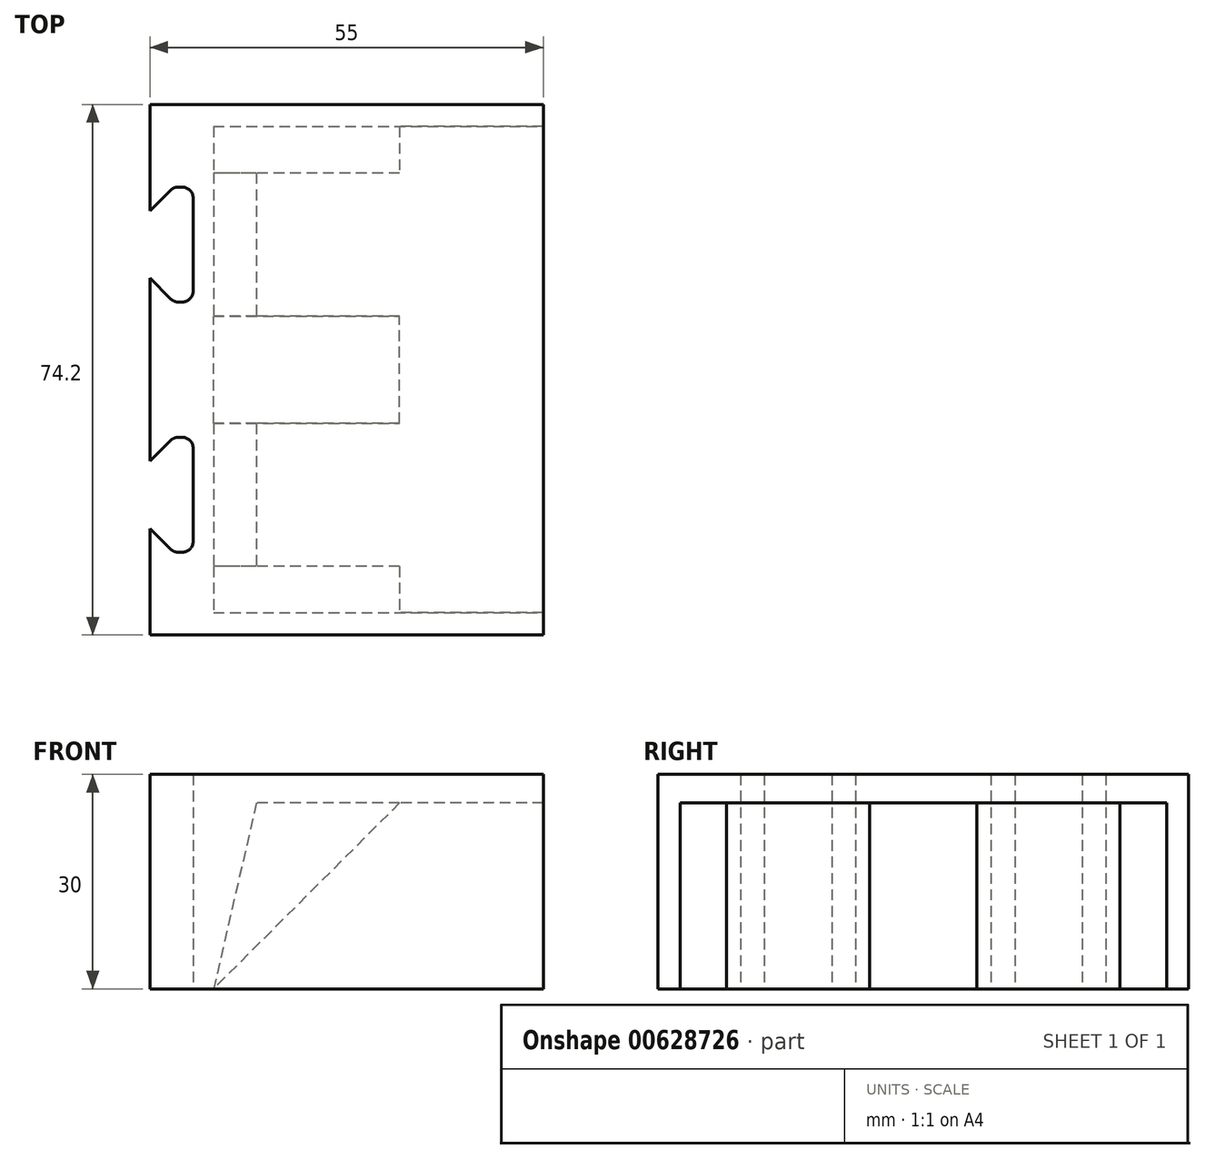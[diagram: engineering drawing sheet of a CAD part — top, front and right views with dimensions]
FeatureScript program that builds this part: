
annotation { "Feature Type Name" : "Feature", "Feature Type Description" : "" }
export const myFeature = defineFeature(function(context is Context, id is Id, definition is map)
    precondition{}
    {
        {
            var Q0;
            Q0=qCreatedBy(makeId("Top.planeOp"),FACE);
            var sketch = newSketch(context, id + "F0", { "sketchPlane" : qUnion([Q0])});
            skLineSegment(sketch, "E0.bottom", {"start": v(90, -35) * mm, "end": v(0, -35) * mm});
            skLineSegment(sketch, "E0.top", {"start": v(90, 35) * mm, "end": v(0, 35) * mm});
            skLineSegment(sketch, "E0.left", {"start": v(90, -35) * mm, "end": v(90, 35) * mm});
            skPoint(sketch, "E0.middle", {"position": v(0, 0) * mm});
            skPoint(sketch, "E1.middle", {"position": v(49.8, 0) * mm});
            skLineSegment(sketch, "E2", {"start": v(0, 0) * mm, "end": v(24, 0) * mm, "construction": true});
            skLineSegment(sketch, "E3", {"start": v(0, 0) * mm, "end": v(0, -14) * mm, "construction": true});
            skLineSegment(sketch, "E4", {"start": v(0, 0) * mm, "end": v(-35, 0) * mm, "construction": true});
            skLineSegment(sketch, "E5.bottom", {"start": v(-5, -19.5) * mm, "end": v(5, -19.5) * mm});
            skLineSegment(sketch, "E5.top", {"start": v(-5, 19.5) * mm, "end": v(5, 19.5) * mm});
            skLineSegment(sketch, "E5.left", {"start": v(-5, -19.5) * mm, "end": v(-5, 19.5) * mm});
            skLineSegment(sketch, "E5.right", {"start": v(5, -19.5) * mm, "end": v(5, 19.5) * mm});
            skLineSegment(sketch, "E6.bottom", {"start": v(-40, -17.25) * mm, "end": v(-30, -17.25) * mm});
            skLineSegment(sketch, "E6.top", {"start": v(-40, 17.25) * mm, "end": v(-30, 17.25) * mm});
            skLineSegment(sketch, "E6.left", {"start": v(-40, -17.25) * mm, "end": v(-40, 17.25) * mm});
            skLineSegment(sketch, "E6.right", {"start": v(-30, -17.25) * mm, "end": v(-30, 17.25) * mm});
            skPoint(sketch, "E6.middle", {"position": v(-35, 0) * mm});
            skLineSegment(sketch, "E7", {"start": v(0, 35) * mm, "end": v(0, 23) * mm});
            skPoint(sketch, "E7.endSnap0", {"position": v(0, 35) * mm});
            skLineSegment(sketch, "E8", {"start": v(0, 23) * mm, "end": v(-50, 23) * mm});
            skLineSegment(sketch, "E9", {"start": v(-50, 23) * mm, "end": v(-50, 0) * mm});
            skLineSegment(sketch, "E10.MirrorCS", {"start": v(-50, -23) * mm, "end": v(-50, 0) * mm});
            skLineSegment(sketch, "E11.MirrorCS", {"start": v(0, -35) * mm, "end": v(0, -23) * mm});
            skLineSegment(sketch, "E12.MirrorCS", {"start": v(0, -23) * mm, "end": v(-50, -23) * mm});
            skPoint(sketch, "E0.right.end.orphan", {"position": v(-90, 35) * mm});
            skPoint(sketch, "E13.orphan", {"position": v(-90, -35) * mm});
            skLineSegment(sketch, "E14.0", {"start": v(92.1, -37.1) * mm, "end": v(92.1, 37.1) * mm});
            skLineSegment(sketch, "E14.1", {"start": v(92.1, -37.1) * mm, "end": v(-2.1, -37.1) * mm});
            skLineSegment(sketch, "E14.2", {"start": v(92.1, 37.1) * mm, "end": v(-2.1, 37.1) * mm});
            skLineSegment(sketch, "E14.3", {"start": v(-2.1, -37.1) * mm, "end": v(-2.1, -25.1) * mm});
            skLineSegment(sketch, "E14.4", {"start": v(-2.1, -25.1) * mm, "end": v(-52.1, -25.1) * mm});
            skLineSegment(sketch, "E14.5", {"start": v(-2.1, 37.1) * mm, "end": v(-2.1, 25.1) * mm});
            skLineSegment(sketch, "E14.6", {"start": v(-2.1, 25.1) * mm, "end": v(-52.1, 25.1) * mm});
            skLineSegment(sketch, "E14.7", {"start": v(-52.1, 25.1) * mm, "end": v(-52.1, 0) * mm});
            skLineSegment(sketch, "E14.8", {"start": v(-52.1, -25.1) * mm, "end": v(-52.1, 0) * mm});
            skLineSegment(sketch, "E15.bottom", {"start": v(-30, 52.75) * mm, "end": v(-40, 52.75) * mm});
            skLineSegment(sketch, "E15.top", {"start": v(-30, 87.25) * mm, "end": v(-40, 87.25) * mm});
            skLineSegment(sketch, "E15.left", {"start": v(-30, 52.75) * mm, "end": v(-30, 87.25) * mm});
            skLineSegment(sketch, "E15.right", {"start": v(-40, 52.75) * mm, "end": v(-40, 87.25) * mm});
            skPoint(sketch, "E15.middle", {"position": v(-35, 70) * mm});
            skLineSegment(sketch, "E16.bottom", {"start": v(-5, 50.5) * mm, "end": v(5, 50.5) * mm});
            skLineSegment(sketch, "E16.top", {"start": v(-5, 89.5) * mm, "end": v(5, 89.5) * mm});
            skLineSegment(sketch, "E16.left", {"start": v(-5, 50.5) * mm, "end": v(-5, 89.5) * mm});
            skLineSegment(sketch, "E16.right", {"start": v(5, 50.5) * mm, "end": v(5, 89.5) * mm});
            skPoint(sketch, "E16.middle", {"position": v(0, 70) * mm});
            skPoint(sketch, "E16.middle.positionSnap0", {"position": v(-30, 70) * mm});
            skPoint(sketch, "E16.centerSnap0", {"position": v(-30, 70) * mm});
            skLineSegment(sketch, "E17", {"start": v(-35, 0) * mm, "end": v(-35, 70) * mm, "construction": true});
            skCircle(sketch, "E18", {"center": v(0, -14) * mm, "radius": 2 * mm});
            skLineSegment(sketch, "E19", {"start": v(-35, 0) * mm, "end": v(-35, -11.75) * mm, "construction": true});
            skCircle(sketch, "E20", {"center": v(-35, -11.75) * mm, "radius": 2 * mm});
            skCircle(sketch, "E21.MirrorC", {"center": v(-35, 11.75) * mm, "radius": 2 * mm});
            skCircle(sketch, "E22.MirrorC", {"center": v(0, 14) * mm, "radius": 2 * mm});
            skLineSegment(sketch, "E23", {"start": v(-35, 70) * mm, "end": v(-35, 81.75) * mm, "construction": true});
            skLineSegment(sketch, "E24", {"start": v(0, 70) * mm, "end": v(0, 84) * mm, "construction": true});
            skCircle(sketch, "E25", {"center": v(-35, 81.75) * mm, "radius": 2 * mm});
            skCircle(sketch, "E26", {"center": v(0, 84) * mm, "radius": 2 * mm});
            skLineSegment(sketch, "E27", {"start": v(-35, 70) * mm, "end": v(-30, 70) * mm, "construction": true});
            skCircle(sketch, "E28.MirrorC", {"center": v(-35, 58.25) * mm, "radius": 2 * mm});
            skCircle(sketch, "E29.MirrorC", {"center": v(0, 56) * mm, "radius": 2 * mm});
            skLineSegment(sketch, "E30", {"start": v(90, -35) * mm, "end": v(92.1, -35) * mm});
            skLineSegment(sketch, "E31", {"start": v(90, 35) * mm, "end": v(92.1, 35) * mm});
            skLineSegment(sketch, "E32", {"start": v(-2.1, 37.1) * mm, "end": v(-6.1, 37.1) * mm});
            skLineSegment(sketch, "E33", {"start": v(-6.1, 37.1) * mm, "end": v(-6.1, 25.1) * mm});
            skLineSegment(sketch, "E34", {"start": v(-2.1, -37.1) * mm, "end": v(-6.1, -37.1) * mm});
            skLineSegment(sketch, "E35", {"start": v(-6.1, -37.1) * mm, "end": v(-6.1, -25.1) * mm});
            skLineSegment(sketch, "E36", {"start": v(-41, 23) * mm, "end": v(-41, 11) * mm});
            skLineSegment(sketch, "E37", {"start": v(-41, 11) * mm, "end": v(-50, 11) * mm});
            skPoint(sketch, "E38.end.orphan", {"position": v(-41, 14.45) * mm});
            skLineSegment(sketch, "E39.MirrorCS", {"start": v(-41, -11) * mm, "end": v(-50, -11) * mm});
            skLineSegment(sketch, "E40.MirrorCS", {"start": v(-41, -23) * mm, "end": v(-41, -11) * mm});
            skLineSegment(sketch, "E41", {"start": v(90, -35) * mm, "end": v(90, -37.1) * mm});
            skLineSegment(sketch, "E42", {"start": v(90, 35) * mm, "end": v(90, 37.1) * mm});
            skLineSegment(sketch, "E43.bottom", {"start": v(90, 35) * mm, "end": v(86, 35) * mm});
            skLineSegment(sketch, "E43.left", {"start": v(90, 35) * mm, "end": v(90, 23) * mm});
            skLineSegment(sketch, "E44.bottom", {"start": v(90, -35) * mm, "end": v(86, -35) * mm});
            skLineSegment(sketch, "E44.left", {"start": v(90, -35) * mm, "end": v(90, -23) * mm});
            skLineSegment(sketch, "E45.bottom", {"start": v(86, -35) * mm, "end": v(80, -35) * mm});
            skLineSegment(sketch, "E46.bottom", {"start": v(86, 35) * mm, "end": v(80, 35) * mm});
            skLineSegment(sketch, "E47.bottom", {"start": v(0, 23) * mm, "end": v(7, 23) * mm});
            skLineSegment(sketch, "E47.top", {"start": v(0, 35) * mm, "end": v(12, 35) * mm});
            skLineSegment(sketch, "E47.left", {"start": v(0, 23) * mm, "end": v(0, 35) * mm});
            skLineSegment(sketch, "E47.right", {"start": v(12, 28) * mm, "end": v(12, 35) * mm});
            skLineSegment(sketch, "E48.bottom", {"start": v(0, -35) * mm, "end": v(12, -35) * mm});
            skLineSegment(sketch, "E48.top", {"start": v(0, -23) * mm, "end": v(7, -23) * mm});
            skLineSegment(sketch, "E48.right", {"start": v(12, -35) * mm, "end": v(12, -28) * mm});
            skCircle(sketch, "E49", {"center": v(6, -29) * mm, "radius": 2 * mm});
            skPoint(sketch, "E49.centerSnap0", {"position": v(6, -35) * mm});
            skPoint(sketch, "E49.centerSnap1", {"position": v(0, -29) * mm});
            skPoint(sketch, "E50.visualSharp", {"position": v(12, -23) * mm});
            skArc(sketch, "E50.filletArc", {"start": v(12, -28) * mm, "mid": v(10.54, -24.46) * mm, "end": v(7, -23) * mm});
            skPoint(sketch, "E51.visualSharp", {"position": v(12, 23) * mm});
            skArc(sketch, "E51.filletArc", {"start": v(7, 23) * mm, "mid": v(10.54, 24.46) * mm, "end": v(12, 28) * mm});
            skCircle(sketch, "E52.MirrorC", {"center": v(6, 29) * mm, "radius": 2 * mm});
            skCircle(sketch, "E53", {"center": v(6, 29) * mm, "radius": 4.5 * mm});
            skCircle(sketch, "E54.MirrorC", {"center": v(6, -29) * mm, "radius": 4.5 * mm});
            skCircle(sketch, "E55", {"center": v(0, 14) * mm, "radius": 6 * mm});
            skCircle(sketch, "E56", {"center": v(-35, 11.75) * mm, "radius": 6 * mm});
            skCircle(sketch, "E57", {"center": v(-35, -11.75) * mm, "radius": 6 * mm});
            skCircle(sketch, "E58", {"center": v(0, -14) * mm, "radius": 6 * mm});
            skLineSegment(sketch, "E59", {"start": v(-6.1, 25.1) * mm, "end": v(-6.08, 23) * mm});
            skLineSegment(sketch, "E60", {"start": v(-6.1, -25.1) * mm, "end": v(-6.1, -23) * mm});
            skLineSegment(sketch, "E61", {"start": v(-47.66, 23) * mm, "end": v(-47.66, 18) * mm, "construction": true});
            skLineSegment(sketch, "E62", {"start": v(-50, 18) * mm, "end": v(-45, 18) * mm, "construction": true});
            skCircle(sketch, "E63", {"center": v(-45, 18) * mm, "radius": 2.25 * mm});
            skCircle(sketch, "E64.MirrorC", {"center": v(-45, -18) * mm, "radius": 2.25 * mm});
            skCircle(sketch, "E65.MirrorC", {"center": v(-25, 18) * mm, "radius": 2.25 * mm});
            skCircle(sketch, "E66.MirrorC", {"center": v(-25, -18) * mm, "radius": 2.25 * mm});
            skCircle(sketch, "E67.MirrorC", {"center": v(28.54, -17.75) * mm, "radius": 2.25 * mm});
            skLineSegment(sketch, "E68.bottom", {"start": v(34.04, -22.75) * mm, "end": v(23.04, -22.75) * mm});
            skLineSegment(sketch, "E68.top", {"start": v(34.04, -12.75) * mm, "end": v(23.04, -12.75) * mm});
            skLineSegment(sketch, "E68.left", {"start": v(36.04, -20.75) * mm, "end": v(36.04, -14.75) * mm});
            skLineSegment(sketch, "E68.right", {"start": v(21.04, -20.75) * mm, "end": v(21.04, -14.75) * mm});
            skLineSegment(sketch, "E69.0", {"start": v(36.44, -12.35) * mm, "end": v(20.64, -12.35) * mm});
            skLineSegment(sketch, "E69.1", {"start": v(36.44, -23.15) * mm, "end": v(36.44, -12.35) * mm});
            skLineSegment(sketch, "E69.2", {"start": v(36.44, -23.15) * mm, "end": v(20.64, -23.15) * mm});
            skLineSegment(sketch, "E69.3", {"start": v(20.64, -23.15) * mm, "end": v(20.64, -12.35) * mm});
            skPoint(sketch, "E70.visualSharp", {"position": v(21.04, -12.75) * mm});
            skArc(sketch, "E70.filletArc", {"start": v(23.04, -12.75) * mm, "mid": v(21.62, -13.33) * mm, "end": v(21.04, -14.75) * mm});
            skPoint(sketch, "E71.visualSharp", {"position": v(36.04, -12.75) * mm});
            skArc(sketch, "E71.filletArc", {"start": v(36.04, -14.75) * mm, "mid": v(35.45, -13.33) * mm, "end": v(34.04, -12.75) * mm});
            skPoint(sketch, "E72.visualSharp", {"position": v(36.04, -22.75) * mm});
            skArc(sketch, "E72.filletArc", {"start": v(34.04, -22.75) * mm, "mid": v(35.45, -22.16) * mm, "end": v(36.04, -20.75) * mm});
            skPoint(sketch, "E73.visualSharp", {"position": v(21.04, -22.75) * mm});
            skArc(sketch, "E73.filletArc", {"start": v(21.04, -20.75) * mm, "mid": v(21.62, -22.16) * mm, "end": v(23.04, -22.75) * mm});
            skArc(sketch, "E74.0", {"start": v(39.54, -14.75) * mm, "mid": v(37.93, -10.86) * mm, "end": v(34.04, -9.25) * mm});
            skLineSegment(sketch, "E74.1", {"start": v(39.54, -20.75) * mm, "end": v(39.54, -14.75) * mm});
            skLineSegment(sketch, "E74.2", {"start": v(34.04, -9.25) * mm, "end": v(23.04, -9.25) * mm});
            skArc(sketch, "E74.3", {"start": v(34.04, -26.25) * mm, "mid": v(37.93, -24.64) * mm, "end": v(39.54, -20.75) * mm});
            skArc(sketch, "E74.4", {"start": v(23.04, -9.25) * mm, "mid": v(19.15, -10.86) * mm, "end": v(17.54, -14.75) * mm});
            skLineSegment(sketch, "E74.5", {"start": v(17.54, -20.75) * mm, "end": v(17.54, -14.75) * mm});
            skArc(sketch, "E74.6", {"start": v(17.54, -20.75) * mm, "mid": v(19.15, -24.64) * mm, "end": v(23.04, -26.25) * mm});
            skLineSegment(sketch, "E74.7", {"start": v(34.04, -26.25) * mm, "end": v(23.04, -26.25) * mm});
            skLineSegment(sketch, "E75", {"start": v(45, 37.1) * mm, "end": v(45, -37.1) * mm});
            skLineSegment(sketch, "E76", {"start": v(45, 31.57) * mm, "end": v(68, 31.57) * mm, "construction": true});
            skLineSegment(sketch, "E77", {"start": v(68, 35) * mm, "end": v(68, -35) * mm});
            skLineSegment(sketch, "E78", {"start": v(12, -28) * mm, "end": v(12, 28) * mm});
            skLineSegment(sketch, "E79", {"start": v(12, 35) * mm, "end": v(12, 37.1) * mm});
            skLineSegment(sketch, "E80", {"start": v(68, 35) * mm, "end": v(68, 37.1) * mm});
            skLineSegment(sketch, "E81", {"start": v(68, 31.57) * mm, "end": v(70.1, 31.57) * mm, "construction": true});
            skLineSegment(sketch, "E82", {"start": v(70.1, 37.1) * mm, "end": v(70.1, -37.1) * mm});
            skLineSegment(sketch, "E83", {"start": v(12, -35) * mm, "end": v(12, -37.1) * mm});
            skLineSegment(sketch, "E84", {"start": v(72.96, 0) * mm, "end": v(72.96, 17.5) * mm, "construction": true});
            skPoint(sketch, "E84.startSnap0", {"position": v(70.1, 0) * mm});
            skLineSegment(sketch, "E85", {"start": v(70.1, 13.5) * mm, "end": v(73.34, 10.26) * mm});
            skPoint(sketch, "E86.end.orphan", {"position": v(71.21, 13.5) * mm});
            skPoint(sketch, "E86.start.orphan", {"position": v(71.21, 17.5) * mm});
            skLineSegment(sketch, "E87", {"start": v(74.05, 9.96) * mm, "end": v(74.64, 9.96) * mm});
            skLineSegment(sketch, "E88", {"start": v(72.96, 17.5) * mm, "end": v(71.21, 17.5) * mm, "construction": true});
            skLineSegment(sketch, "E89.MirrorCS", {"start": v(70.1, 21.5) * mm, "end": v(73.34, 24.74) * mm});
            skLineSegment(sketch, "E90.MirrorCS", {"start": v(74.05, 25.04) * mm, "end": v(74.64, 25.04) * mm});
            skLineSegment(sketch, "E91", {"start": v(75.64, 24.04) * mm, "end": v(75.64, 10.96) * mm});
            skPoint(sketch, "E92.visualSharp", {"position": v(75.64, 25.04) * mm});
            skArc(sketch, "E92.filletArc", {"start": v(75.64, 24.04) * mm, "mid": v(75.34, 24.74) * mm, "end": v(74.64, 25.04) * mm});
            skPoint(sketch, "E93.visualSharp", {"position": v(73.64, 25.04) * mm});
            skArc(sketch, "E93.filletArc", {"start": v(74.05, 25.04) * mm, "mid": v(73.67, 24.96) * mm, "end": v(73.34, 24.74) * mm});
            skPoint(sketch, "E94.visualSharp", {"position": v(73.64, 9.96) * mm});
            skArc(sketch, "E94.filletArc", {"start": v(73.34, 10.26) * mm, "mid": v(73.67, 10.04) * mm, "end": v(74.05, 9.96) * mm});
            skPoint(sketch, "E95.visualSharp", {"position": v(75.64, 9.96) * mm});
            skArc(sketch, "E95.filletArc", {"start": v(74.64, 9.96) * mm, "mid": v(75.34, 10.26) * mm, "end": v(75.64, 10.96) * mm});
            skLineSegment(sketch, "E96.MirrorCS", {"start": v(70.1, -13.5) * mm, "end": v(73.34, -10.26) * mm});
            skArc(sketch, "E97.MirrorCS", {"start": v(73.34, -10.26) * mm, "mid": v(73.67, -10.04) * mm, "end": v(74.05, -9.96) * mm});
            skLineSegment(sketch, "E98.MirrorCS", {"start": v(74.05, -9.96) * mm, "end": v(74.64, -9.96) * mm});
            skArc(sketch, "E99.MirrorCS", {"start": v(74.64, -9.96) * mm, "mid": v(75.34, -10.26) * mm, "end": v(75.64, -10.96) * mm});
            skLineSegment(sketch, "E100.MirrorCS", {"start": v(75.64, -24.04) * mm, "end": v(75.64, -10.96) * mm});
            skLineSegment(sketch, "E101.MirrorCS", {"start": v(70.1, -21.5) * mm, "end": v(73.34, -24.74) * mm});
            skArc(sketch, "E102.MirrorCS", {"start": v(74.05, -25.04) * mm, "mid": v(73.67, -24.96) * mm, "end": v(73.34, -24.74) * mm});
            skLineSegment(sketch, "E103.MirrorCS", {"start": v(74.05, -25.04) * mm, "end": v(74.64, -25.04) * mm});
            skArc(sketch, "E104.MirrorCS", {"start": v(75.64, -24.04) * mm, "mid": v(75.34, -24.74) * mm, "end": v(74.64, -25.04) * mm});
            skLineSegment(sketch, "E105", {"start": v(68, -35) * mm, "end": v(56.64, -23.64) * mm, "construction": true});
            skArc(sketch, "E106.MirrorCS", {"start": v(43.26, -40.34) * mm, "mid": v(43.04, -40.67) * mm, "end": v(42.96, -41.05) * mm});
            skArc(sketch, "E107.MirrorCS", {"start": v(58.04, -41.05) * mm, "mid": v(57.96, -40.67) * mm, "end": v(57.74, -40.34) * mm});
            skArc(sketch, "E108.MirrorCS", {"start": v(42.96, -41.64) * mm, "mid": v(43.26, -42.34) * mm, "end": v(43.96, -42.64) * mm});
            skArc(sketch, "E109.MirrorCS", {"start": v(57.04, -42.64) * mm, "mid": v(57.74, -42.34) * mm, "end": v(58.04, -41.64) * mm});
            skLineSegment(sketch, "E110.MirrorCS", {"start": v(42.96, -41.05) * mm, "end": v(42.96, -41.64) * mm});
            skLineSegment(sketch, "E111.MirrorCS", {"start": v(58.04, -41.05) * mm, "end": v(58.04, -41.64) * mm});
            skLineSegment(sketch, "E112.MirrorCS", {"start": v(57.04, -42.64) * mm, "end": v(43.96, -42.64) * mm});
            skLineSegment(sketch, "E113.MirrorCS", {"start": v(46.5, -37.1) * mm, "end": v(43.26, -40.34) * mm});
            skLineSegment(sketch, "E114.MirrorCS", {"start": v(54.5, -37.1) * mm, "end": v(57.74, -40.34) * mm});
            skLineSegment(sketch, "E115", {"start": v(36.04, -37.1) * mm, "end": v(36.04, -40.15) * mm, "construction": true});
            skLineSegment(sketch, "E116.MirrorCS", {"start": v(14.04, -41.05) * mm, "end": v(14.04, -41.64) * mm});
            skArc(sketch, "E117.MirrorCS", {"start": v(14.04, -41.05) * mm, "mid": v(14.12, -40.67) * mm, "end": v(14.33, -40.34) * mm});
            skLineSegment(sketch, "E118.MirrorCS", {"start": v(29.11, -41.05) * mm, "end": v(29.11, -41.64) * mm});
            skArc(sketch, "E119.MirrorCS", {"start": v(28.82, -40.34) * mm, "mid": v(29.04, -40.67) * mm, "end": v(29.11, -41.05) * mm});
            skArc(sketch, "E120.MirrorCS", {"start": v(15.04, -42.64) * mm, "mid": v(14.33, -42.34) * mm, "end": v(14.04, -41.64) * mm});
            skLineSegment(sketch, "E121.MirrorCS", {"start": v(15.04, -42.64) * mm, "end": v(28.11, -42.64) * mm});
            skArc(sketch, "E122.MirrorCS", {"start": v(29.11, -41.64) * mm, "mid": v(28.82, -42.34) * mm, "end": v(28.11, -42.64) * mm});
            skLineSegment(sketch, "E123.MirrorCS", {"start": v(17.58, -37.1) * mm, "end": v(14.33, -40.34) * mm});
            skLineSegment(sketch, "E124.MirrorCS", {"start": v(25.58, -37.1) * mm, "end": v(28.82, -40.34) * mm});
            skLineSegment(sketch, "E125", {"start": v(28.54, -17.75) * mm, "end": v(28.54, 0) * mm, "construction": true});
            skLineSegment(sketch, "E126", {"start": v(28.54, 0) * mm, "end": v(56.04, 0) * mm, "construction": true});
            skLineSegment(sketch, "E127.bottom", {"start": v(53.54, 20) * mm, "end": v(58.54, 20) * mm});
            skLineSegment(sketch, "E127.top", {"start": v(53.54, -20) * mm, "end": v(58.54, -20) * mm});
            skLineSegment(sketch, "E127.left", {"start": v(53.54, 20) * mm, "end": v(53.54, -20) * mm});
            skLineSegment(sketch, "E127.right", {"start": v(58.54, 20) * mm, "end": v(58.54, -20) * mm});
            skPoint(sketch, "E127.middle", {"position": v(56.04, 0) * mm});
            skLineSegment(sketch, "E128", {"start": v(28.54, -17.75) * mm, "end": v(28.54, -35) * mm, "construction": true});
            skPoint(sketch, "E128.endSnap0", {"position": v(28.54, -26.25) * mm});
            skLineSegment(sketch, "E129", {"start": v(28.54, -17.75) * mm, "end": v(12, -17.75) * mm, "construction": true});
            skLineSegment(sketch, "E130", {"start": v(12, 17.54) * mm, "end": v(28.54, 17.54) * mm, "construction": true});
            skLineSegment(sketch, "E131", {"start": v(28.54, 17.54) * mm, "end": v(28.54, 35) * mm, "construction": true});
            skArc(sketch, "E132.MirrorCS", {"start": v(36.04, 14.75) * mm, "mid": v(35.45, 13.33) * mm, "end": v(34.04, 12.75) * mm});
            skArc(sketch, "E133.MirrorCS", {"start": v(23.04, 12.75) * mm, "mid": v(21.62, 13.33) * mm, "end": v(21.04, 14.75) * mm});
            skArc(sketch, "E134.MirrorCS", {"start": v(21.04, 20.75) * mm, "mid": v(21.62, 22.16) * mm, "end": v(23.04, 22.75) * mm});
            skArc(sketch, "E135.MirrorCS", {"start": v(34.04, 22.75) * mm, "mid": v(35.45, 22.16) * mm, "end": v(36.04, 20.75) * mm});
            skArc(sketch, "E136.MirrorCS", {"start": v(23.04, 9.25) * mm, "mid": v(19.15, 10.86) * mm, "end": v(17.54, 14.75) * mm});
            skLineSegment(sketch, "E137.MirrorCS", {"start": v(34.04, 9.25) * mm, "end": v(23.04, 9.25) * mm});
            skPoint(sketch, "E138.MirrorP", {"position": v(36.04, 12.75) * mm});
            skArc(sketch, "E139.MirrorCS", {"start": v(34.04, 26.25) * mm, "mid": v(37.93, 24.64) * mm, "end": v(39.54, 20.75) * mm});
            skArc(sketch, "E140.MirrorCS", {"start": v(17.54, 20.75) * mm, "mid": v(19.15, 24.64) * mm, "end": v(23.04, 26.25) * mm});
            skPoint(sketch, "E141.MirrorP", {"position": v(28.54, 17.75) * mm});
            skLineSegment(sketch, "E142.MirrorCS", {"start": v(36.44, 23.15) * mm, "end": v(20.64, 23.15) * mm});
            skPoint(sketch, "E143.MirrorP", {"position": v(21.04, 12.75) * mm});
            skLineSegment(sketch, "E144.MirrorCS", {"start": v(34.04, 26.25) * mm, "end": v(23.04, 26.25) * mm});
            skPoint(sketch, "E145.MirrorP", {"position": v(21.04, 22.75) * mm});
            skLineSegment(sketch, "E146.MirrorCS", {"start": v(20.64, 23.15) * mm, "end": v(20.64, 12.35) * mm});
            skLineSegment(sketch, "E147.MirrorCS", {"start": v(36.44, 12.35) * mm, "end": v(20.64, 12.35) * mm});
            skLineSegment(sketch, "E148.MirrorCS", {"start": v(17.54, 20.75) * mm, "end": v(17.54, 14.75) * mm});
            skCircle(sketch, "E149.MirrorC", {"center": v(28.54, 17.75) * mm, "radius": 2.25 * mm});
            skPoint(sketch, "E150.MirrorP", {"position": v(28.54, 26.25) * mm});
            skPoint(sketch, "E151.MirrorP", {"position": v(36.04, 22.75) * mm});
            skLineSegment(sketch, "E152.MirrorCS", {"start": v(21.04, 20.75) * mm, "end": v(21.04, 14.75) * mm});
            skLineSegment(sketch, "E153.MirrorCS", {"start": v(39.54, 20.75) * mm, "end": v(39.54, 14.75) * mm});
            skLineSegment(sketch, "E154.MirrorCS", {"start": v(36.44, 23.15) * mm, "end": v(36.44, 12.35) * mm});
            skLineSegment(sketch, "E155.MirrorCS", {"start": v(34.04, 22.75) * mm, "end": v(23.04, 22.75) * mm});
            skArc(sketch, "E156.MirrorCS", {"start": v(39.54, 14.75) * mm, "mid": v(37.93, 10.86) * mm, "end": v(34.04, 9.25) * mm});
            skLineSegment(sketch, "E157.MirrorCS", {"start": v(34.04, 12.75) * mm, "end": v(23.04, 12.75) * mm});
            skLineSegment(sketch, "E158.MirrorCS", {"start": v(36.04, 20.75) * mm, "end": v(36.04, 14.75) * mm});
            skArc(sketch, "E159.MirrorCS", {"start": v(29.11, 41.64) * mm, "mid": v(28.82, 42.34) * mm, "end": v(28.11, 42.64) * mm});
            skArc(sketch, "E160.MirrorCS", {"start": v(28.82, 40.34) * mm, "mid": v(29.04, 40.67) * mm, "end": v(29.11, 41.05) * mm});
            skArc(sketch, "E161.MirrorCS", {"start": v(15.04, 42.64) * mm, "mid": v(14.33, 42.34) * mm, "end": v(14.04, 41.64) * mm});
            skArc(sketch, "E162.MirrorCS", {"start": v(14.04, 41.05) * mm, "mid": v(14.12, 40.67) * mm, "end": v(14.33, 40.34) * mm});
            skArc(sketch, "E163.MirrorCS", {"start": v(57.04, 42.64) * mm, "mid": v(57.74, 42.34) * mm, "end": v(58.04, 41.64) * mm});
            skArc(sketch, "E164.MirrorCS", {"start": v(58.04, 41.05) * mm, "mid": v(57.96, 40.67) * mm, "end": v(57.74, 40.34) * mm});
            skLineSegment(sketch, "E165.MirrorCS", {"start": v(42.96, 41.05) * mm, "end": v(42.96, 41.64) * mm});
            skLineSegment(sketch, "E166.MirrorCS", {"start": v(58.04, 41.05) * mm, "end": v(58.04, 41.64) * mm});
            skLineSegment(sketch, "E167.MirrorCS", {"start": v(14.04, 41.05) * mm, "end": v(14.04, 41.64) * mm});
            skLineSegment(sketch, "E168.MirrorCS", {"start": v(29.11, 41.05) * mm, "end": v(29.11, 41.64) * mm});
            skArc(sketch, "E169.MirrorCS", {"start": v(42.96, 41.64) * mm, "mid": v(43.26, 42.34) * mm, "end": v(43.96, 42.64) * mm});
            skArc(sketch, "E170.MirrorCS", {"start": v(43.26, 40.34) * mm, "mid": v(43.04, 40.67) * mm, "end": v(42.96, 41.05) * mm});
            skLineSegment(sketch, "E171.MirrorCS", {"start": v(57.04, 42.64) * mm, "end": v(43.96, 42.64) * mm});
            skLineSegment(sketch, "E172.MirrorCS", {"start": v(15.04, 42.64) * mm, "end": v(28.11, 42.64) * mm});
            skLineSegment(sketch, "E173.MirrorCS", {"start": v(17.58, 37.1) * mm, "end": v(14.33, 40.34) * mm});
            skLineSegment(sketch, "E174.MirrorCS", {"start": v(25.58, 37.1) * mm, "end": v(28.82, 40.34) * mm});
            skLineSegment(sketch, "E175.MirrorCS", {"start": v(46.5, 37.1) * mm, "end": v(43.26, 40.34) * mm});
            skLineSegment(sketch, "E176.MirrorCS", {"start": v(54.5, 37.1) * mm, "end": v(57.74, 40.34) * mm});
            skLineSegment(sketch, "E177", {"start": v(92.1, 37.1) * mm, "end": v(125.1, 37.1) * mm});
            skLineSegment(sketch, "E178", {"start": v(125.1, 37.1) * mm, "end": v(125.1, -37.1) * mm});
            skLineSegment(sketch, "E179", {"start": v(125.1, -37.1) * mm, "end": v(92.1, -37.1) * mm});
            skLineSegment(sketch, "E180", {"start": v(125.1, 30.14) * mm, "end": v(123, 30.14) * mm, "construction": true});
            skLineSegment(sketch, "E181.0", {"start": v(70.1, 12.8) * mm, "end": v(72.99, 9.9) * mm});
            skArc(sketch, "E181.1", {"start": v(72.99, 9.9) * mm, "mid": v(73.48, 9.58) * mm, "end": v(74.05, 9.46) * mm});
            skLineSegment(sketch, "E181.2", {"start": v(74.05, 9.46) * mm, "end": v(74.64, 9.46) * mm});
            skArc(sketch, "E181.3", {"start": v(74.64, 9.46) * mm, "mid": v(75.7, 9.9) * mm, "end": v(76.14, 10.96) * mm});
            skLineSegment(sketch, "E181.4", {"start": v(76.14, 24.04) * mm, "end": v(76.14, 10.96) * mm});
            skLineSegment(sketch, "E181.5", {"start": v(70.1, 22.2) * mm, "end": v(72.99, 25.1) * mm});
            skArc(sketch, "E181.6", {"start": v(74.05, 25.54) * mm, "mid": v(73.48, 25.42) * mm, "end": v(72.99, 25.1) * mm});
            skLineSegment(sketch, "E181.7", {"start": v(74.05, 25.54) * mm, "end": v(74.64, 25.54) * mm});
            skArc(sketch, "E181.8", {"start": v(76.14, 24.04) * mm, "mid": v(75.7, 25.1) * mm, "end": v(74.64, 25.54) * mm});
            skLineSegment(sketch, "E182.MirrorCS", {"start": v(70.1, -12.8) * mm, "end": v(72.99, -9.9) * mm});
            skArc(sketch, "E183.MirrorCS", {"start": v(72.99, -9.9) * mm, "mid": v(73.48, -9.58) * mm, "end": v(74.05, -9.46) * mm});
            skLineSegment(sketch, "E184.MirrorCS", {"start": v(74.05, -9.46) * mm, "end": v(74.64, -9.46) * mm});
            skArc(sketch, "E185.MirrorCS", {"start": v(74.64, -9.46) * mm, "mid": v(75.7, -9.9) * mm, "end": v(76.14, -10.96) * mm});
            skLineSegment(sketch, "E186.MirrorCS", {"start": v(76.14, -24.04) * mm, "end": v(76.14, -10.96) * mm});
            skArc(sketch, "E187.MirrorCS", {"start": v(76.14, -24.04) * mm, "mid": v(75.7, -25.1) * mm, "end": v(74.64, -25.54) * mm});
            skLineSegment(sketch, "E188.MirrorCS", {"start": v(74.05, -25.54) * mm, "end": v(74.64, -25.54) * mm});
            skArc(sketch, "E189.MirrorCS", {"start": v(74.05, -25.54) * mm, "mid": v(73.48, -25.42) * mm, "end": v(72.99, -25.1) * mm});
            skLineSegment(sketch, "E190.MirrorCS", {"start": v(70.1, -22.2) * mm, "end": v(72.99, -25.1) * mm});
            skLineSegment(sketch, "E191.0", {"start": v(45.8, -37.1) * mm, "end": v(42.9, -39.99) * mm});
            skArc(sketch, "E191.1", {"start": v(42.9, -39.99) * mm, "mid": v(42.58, -40.48) * mm, "end": v(42.46, -41.05) * mm});
            skLineSegment(sketch, "E191.2", {"start": v(42.46, -41.05) * mm, "end": v(42.46, -41.64) * mm});
            skArc(sketch, "E191.3", {"start": v(42.46, -41.64) * mm, "mid": v(42.9, -42.7) * mm, "end": v(43.96, -43.14) * mm});
            skLineSegment(sketch, "E191.4", {"start": v(57.04, -43.14) * mm, "end": v(43.96, -43.14) * mm});
            skLineSegment(sketch, "E191.5", {"start": v(55.2, -37.1) * mm, "end": v(58.1, -39.99) * mm});
            skArc(sketch, "E191.6", {"start": v(58.54, -41.05) * mm, "mid": v(58.42, -40.48) * mm, "end": v(58.1, -39.99) * mm});
            skLineSegment(sketch, "E191.7", {"start": v(58.54, -41.05) * mm, "end": v(58.54, -41.64) * mm});
            skArc(sketch, "E191.8", {"start": v(57.04, -43.14) * mm, "mid": v(58.1, -42.7) * mm, "end": v(58.54, -41.64) * mm});
            skLineSegment(sketch, "E192.MirrorCS", {"start": v(26.28, -37.1) * mm, "end": v(29.17, -39.99) * mm});
            skArc(sketch, "E193.MirrorCS", {"start": v(29.17, -39.99) * mm, "mid": v(29.5, -40.48) * mm, "end": v(29.61, -41.05) * mm});
            skLineSegment(sketch, "E194.MirrorCS", {"start": v(29.61, -41.05) * mm, "end": v(29.61, -41.64) * mm});
            skArc(sketch, "E195.MirrorCS", {"start": v(29.61, -41.64) * mm, "mid": v(29.17, -42.7) * mm, "end": v(28.11, -43.14) * mm});
            skLineSegment(sketch, "E196.MirrorCS", {"start": v(15.04, -43.14) * mm, "end": v(28.11, -43.14) * mm});
            skArc(sketch, "E197.MirrorCS", {"start": v(15.04, -43.14) * mm, "mid": v(13.98, -42.7) * mm, "end": v(13.54, -41.64) * mm});
            skLineSegment(sketch, "E198.MirrorCS", {"start": v(13.54, -41.05) * mm, "end": v(13.54, -41.64) * mm});
            skArc(sketch, "E199.MirrorCS", {"start": v(13.54, -41.05) * mm, "mid": v(13.66, -40.48) * mm, "end": v(13.98, -39.99) * mm});
            skLineSegment(sketch, "E200.MirrorCS", {"start": v(16.87, -37.1) * mm, "end": v(13.98, -39.99) * mm});
            skSolve(sketch);
        }
        {
            var Q0;
            Q0=makeQuery(id+"F0.imprint","IMPRINT",FACE,{"disambiguationData":[TD([[makeQuery(id+"F0.imprint","IMPRINT",EDGE,{"derivedFrom":sQuery(id+"F0.wireOp",EDGE,"E0.left")}),1.0]])]});
            var Q1;
            {var subQ0=sQuery(id+"F0.wireOp",EDGE,"E42");Q1=makeQuery(id+"F0.imprint","IMPRINT",FACE,{"disambiguationData":[TD([[makeQuery(id+"F0.imprint","IMPRINT",EDGE,{"derivedFrom":subQ0}),1.0]])]});}
            var Q2;
            Q2=makeQuery(id+"F0.imprint","IMPRINT",FACE,{"disambiguationData":[TD([[makeQuery(id+"F0.imprint","IMPRINT",EDGE,{"derivedFrom":sQuery(id+"F0.wireOp",EDGE,"E0.left")}),-1.0]])]});
            var Q3;
            {var subQ3=sQuery(id+"F0.wireOp",EDGE,"E31");Q3=makeQuery(id+"F0.imprint","IMPRINT",FACE,{"disambiguationData":[TD([[makeQuery(id+"F0.imprint","IMPRINT",EDGE,{"derivedFrom":subQ3}),1.0]])]});}
            var Q4;
            {var subQ0=sQuery(id+"F0.wireOp",EDGE,"E177");Q4=makeQuery(id+"F0.imprint","IMPRINT",FACE,{"disambiguationData":[TD([[makeQuery(id+"F0.imprint","IMPRINT",EDGE,{"derivedFrom":subQ0}),-1.0]])]});}
            var Q5;
            {var subQ5=sQuery(id+"F0.wireOp",EDGE,"E41");Q5=makeQuery(id+"F0.imprint","IMPRINT",FACE,{"disambiguationData":[TD([[makeQuery(id+"F0.imprint","IMPRINT",EDGE,{"derivedFrom":subQ5}),-1.0]])]});}
            var Q6;
            {var subQ3=sQuery(id+"F0.wireOp",EDGE,"E30");Q6=makeQuery(id+"F0.imprint","IMPRINT",FACE,{"disambiguationData":[TD([[makeQuery(id+"F0.imprint","IMPRINT",EDGE,{"derivedFrom":subQ3}),-1.0]])]});}
            extrude(context, id + "F1", {"entities" : qUnion([Q0, Q1, Q2, Q3, Q4, Q5, Q6]), "depth" : 30 * mm});
        }
        {
            var Q0;
            Q0=qCreatedBy(makeId("Top.planeOp"),FACE);
            cPlane(context, id + "F2", {"entities" : qUnion([Q0]), "cplaneType" : CPlaneType.OFFSET, "offset" : 10 * mm, "width" : 150 * mm, "height" : 150 * mm});
        }
        {
            var Q0;
            Q0=qCreatedBy(makeId("Front.planeOp"),FACE);
            var sketch = newSketch(context, id + "F3", { "sketchPlane" : qUnion([Q0])});
            skLineSegment(sketch, "E201", {"start": v(0, 0) * mm, "end": v(79, 0) * mm, "construction": true});
            skLineSegment(sketch, "E202", {"start": v(79, 0) * mm, "end": v(125.1, 0) * mm});
            skLineSegment(sketch, "E203", {"start": v(125.1, 0) * mm, "end": v(125.1, 26) * mm});
            skLineSegment(sketch, "E204", {"start": v(79, 0) * mm, "end": v(105, 26) * mm});
            skLineSegment(sketch, "E205", {"start": v(125.1, 26) * mm, "end": v(105, 26) * mm});
            skLineSegment(sketch, "E206", {"start": v(105, 26) * mm, "end": v(85, 26) * mm});
            skLineSegment(sketch, "E207", {"start": v(85, 26) * mm, "end": v(79, 0) * mm});
            skSolve(sketch);
        }
        {
            var Q0;
            Q0=makeQuery(id+"F3.imprint","IMPRINT",FACE,{"disambiguationData":[TD([[makeQuery(id+"F3.imprint","IMPRINT",EDGE,{"derivedFrom":sQuery(id+"F3.wireOp",EDGE,"E202")}),1.0]])]});
            extrude(context, id + "F4", {"entities" : qUnion([Q0]), "operationType" : NewBodyOperationType.REMOVE, "endBound" : BoundingType.SYMMETRIC, "oppositeDirection" : true, "depth" : 68 * mm});
        }
        {
            var Q0;
            Q0=qSketchRegion(id+"F3",true);
            extrude(context, id + "F5", {"entities" : qUnion([Q0]), "operationType" : NewBodyOperationType.REMOVE, "endBound" : BoundingType.SYMMETRIC, "oppositeDirection" : true, "depth" : 55 * mm});
        }
        {
            var Q0;
            Q0=makeQuery(id+"F3.imprint","IMPRINT",FACE,{"disambiguationData":[TD([[makeQuery(id+"F3.imprint","IMPRINT",EDGE,{"derivedFrom":sQuery(id+"F3.wireOp",EDGE,"E204")}),1.0]])]});
            extrude(context, id + "F6", {"entities" : qUnion([Q0]), "operationType" : NewBodyOperationType.ADD, "endBound" : BoundingType.SYMMETRIC, "depth" : 15 * mm});
        }
    });
